# Revit family: Domotics-CablaggioStrutturato-GEWISS-QUADRI_PAVIMENTO_19_30U_P600
name_source: partatom
category: Apparecchi elettrici
units: mm (PartAtom-declared; Revit-internal decimal feet)

## family parameters
Condiviso = No
Host = Superficie
Mantenere orientamento annotazione = Sì
Numero OmniClass = 23.80.30.00
Punto di calcolo locali = Sì
Quota connettore circolare = Usa diametro
Taglio con vuoti quando caricato = No
Tipo di parte = Normale
Titolo OmniClass = Distribution Devices

## types (1)
- Domotics-CablaggioStrutturato-GEWISS-QUADRI_PAVIMENTO_19_30U_P600
    Apertura porta = 135°
    Catalogo = DOMOTICS
    Categoria = Armadio da pavimento 19"
    Codice Electrocod = 3752
    Colore = Grigio (RAL 7035)
    Descrizione = ARMADIO DA PAVIMENTO 19 30U 600x600MM
    Dim. esterne BxHxP (mm) = 600x1485x600
    Finitura = Bucciata
    Grado di protezione = IP20
    IDF = 85012eda-62a1-487c-af3f-200afc351462
    IDT = 39e0a6a38c734b9c98aba4b4c497b8be
    Immagine tipo = C.jpg
    Materiale = Acciaio
    Modello = GW38452
    N. montanti = 2
    Portata statica = 1000KG
    Produttore = GEWISS S.p.A.
    Profondità (mm) = 600 mm
    Prospetto di default = 900 mm  [stored 2.95276 ft]
    SEO = Armadio LAN
    Scheda Tecnica = https://www.gewiss.com
    Tipologia porta = Reversibile
    URL = https://www.gewiss.com
    Unità di cablaggio = 30 U
    Versione file RFA = 21.2
    barra din = Sì
    n_poli = 1

note: [stored X ft] marks values corroborated as IEEE doubles in the binary element streams (Revit-internal decimal feet)

## geometry (parser evidence)
native form markers: Sweep x3
no freeform markers — native parametric forms only
